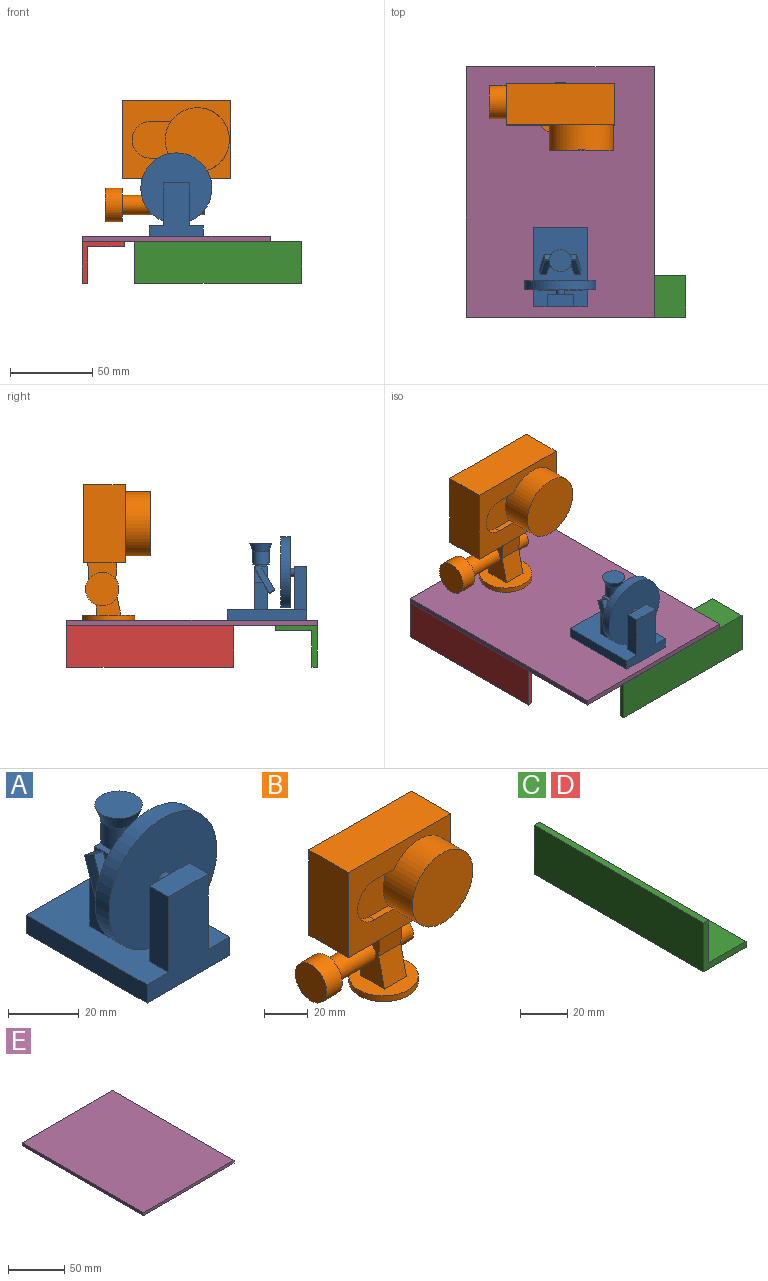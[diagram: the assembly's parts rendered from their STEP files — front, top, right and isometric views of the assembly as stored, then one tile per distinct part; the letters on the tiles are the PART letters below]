
ASSEMBLY  parts=5 mates=4
PART A: 46 faces, bbox 43.2x48.3x50.8 mm
  f0: plane 8.44x4.96mm, normal (-0.98,0,0.18), area 21.3mm2, adj f17,f20,f39
  f1: plane 3.03x1.72mm, normal (-0.98,0,0.18), area 2.6mm2, adj f20,f25,f43
  f2: plane 7.17x4.21mm, normal (0.98,0,0.18), area 15.4mm2, adj f18,f25,f33
  f3: plane 48.26x6.35mm, normal (-1,0,0), area 306.5mm2, adj f4,f6,f7,f8
  f4: plane 33.02x32.51mm, normal (0,-1,0), area 628.3mm2, adj f3,f5,f7,f8,f9,f10,f11
  f5: plane 48.26x6.35mm, normal (1,0,0), area 306.5mm2, adj f4,f6,f7,f8
  f6: plane 33.02x6.35mm, normal (0,1,0), area 209.7mm2, adj f3,f5,f7,f8
  f7: plane 48.26x33.02mm, normal (0,0,1), area 1374.8mm2, adj f3,f4,f5,f6,f9,f10,f12,f17
  f8: plane 48.26x33.02mm, normal (0,0,-1), area 1593.5mm2, adj f3,f4,f5,f6
  f9: plane 26.16x7.62mm, normal (-1,0,0), area 199.4mm2, adj f4,f7,f11,f12
  f10: plane 26.16x7.62mm, normal (1,0,0), area 199.4mm2, adj f4,f7,f11,f12
  f11: plane 16x7.62mm, normal (0,0,1), area 121.9mm2, adj f4,f9,f10,f12
  f12: plane 26.16x16mm, normal (0,1,0), area 398.4mm2, adj f7,f9,f10,f11,f13
  f13: cylinder r=2.54mm len=5.08mm, axis (0,-1,0), area 40.5mm2, adj f12,f16
  f14: cylinder r=21.59mm len=43.18mm, axis (0,-1,0), area 758mm2, adj f15,f16
  f15: plane 43.18x43.18mm, normal (0,1,0), area 1464.4mm2, adj f14
  f16: plane 43.18x43.18mm, normal (0,-1,0), area 1444.1mm2, adj f13,f14
  f17: plane 16.51x7.62mm, normal (-1,0,0), area 125.8mm2, adj f0,f7,f18,f20,f45
  f18: plane 26.67x15.24mm, normal (0,-1,0), area 361.3mm2, adj f2,f7,f17,f19,f21,f22,f23,f24
  f19: plane 10.16x7.62mm, normal (1,0,0), area 77.4mm2, adj f7,f18,f20,f23
  f20: plane 26.67x15.24mm, normal (0,1,0), area 361.3mm2, adj f0,f1,f7,f17,f19,f21,f22,f23
  f21: plane 10.16x7.62mm, normal (-1,0,0), area 77.4mm2, adj f7,f18,f20,f23
  f22: plane 16.51x7.62mm, normal (1,0,0), area 125.8mm2, adj f7,f18,f20,f26,f38
  f23: plane 7.62x2.54mm, normal (0,0,-1), area 19.4mm2, adj f18,f19,f20,f21
  f24: plane 7.2x4.23mm, normal (-0.98,0,0.18), area 15.5mm2, adj f18,f25,f41
  f25: plane 11.43x7.62mm, normal (0,0,1), area 47.4mm2, adj f1,f2,f18,f20,f24,f26,f27,f32
  f26: plane 10.16x4.98mm, normal (0.98,0,0.18), area 24.1mm2, adj f20,f22,f25,f35,f36
  f27: cylinder r=3.56mm len=7.11mm, axis (0,0,-1), area 28.4mm2, adj f25,f29
  f28: cylinder r=5.08mm len=10.16mm, axis (0,0,-1), area 243.2mm2, adj f29,f30
  f29: plane 10.16x10.16mm, normal (0,0,-1), area 41.3mm2, adj f27,f28
  f30: cone r=5.08mm half-angle=20deg, axis (0,0,1), area 180.7mm2, adj f28,f31
  f31: plane 13.49x13.49mm, normal (0,0,1), area 142.9mm2, adj f30
  f32: plane 3.74x0.7mm, normal (-0.18,0,0.98), area 1.4mm2, adj f25,f33,f36,f37
  f33: plane 15.65x8.78mm, normal (-0.09,-0.87,0.49), area 66.9mm2, adj f2,f32,f34,f37,f38
  f34: plane 4.1x3.3mm, normal (0.16,-0.5,-0.85), area 14.5mm2, adj f33,f35,f37,f38
  f35: plane 15.81x8.88mm, normal (0.09,0.87,-0.49), area 67.6mm2, adj f26,f34,f36,f37,f38
  f36: plane 4.07x3.02mm, normal (-0.16,0.5,0.85), area 13.3mm2, adj f26,f32,f35,f37
  f37: plane 16.82x12.18mm, normal (0.98,0,0.18), area 67.6mm2, adj f32,f33,f34,f35,f36
  f38: plane 9.66x7.21mm, normal (-0.98,0,-0.18), area 28.3mm2, adj f18,f22,f33,f34,f35
  f39: plane 15.84x8.89mm, normal (-0.09,0.87,-0.49), area 67.7mm2, adj f0,f40,f43,f44,f45
  f40: plane 4.1x3.3mm, normal (-0.16,-0.5,-0.85), area 14.5mm2, adj f39,f41,f44,f45
  f41: plane 15.68x8.8mm, normal (0.09,-0.87,0.49), area 67mm2, adj f24,f40,f42,f44,f45
  f42: plane 3.74x0.7mm, normal (0.18,0,0.98), area 1.4mm2, adj f25,f41,f43,f44
  f43: plane 4.07x3.03mm, normal (0.16,0.5,0.85), area 13.3mm2, adj f1,f39,f42,f44
  f44: plane 16.85x12.19mm, normal (-0.98,0,0.18), area 67.7mm2, adj f39,f40,f41,f42,f43
  f45: plane 9.65x7.23mm, normal (0.98,0,-0.18), area 28.4mm2, adj f17,f18,f39,f40,f41
PART B: 33 faces, bbox 76.2x41.3x82.6 mm
  f0: plane 66.04x47.63mm, normal (0,1,0), area 2919.3mm2, adj f1,f2,f3,f4,f12,f13,f14,f15
  f1: plane 47.63x25.4mm, normal (-1,0,0), area 1209.7mm2, adj f0,f2,f4,f5
  f2: plane 66.04x25.4mm, normal (0,0,-1), area 1424.5mm2, adj f0,f1,f3,f5,f17,f18,f22,f23
  f3: plane 47.63x25.4mm, normal (1,0,0), area 1209.7mm2, adj f0,f2,f4,f5
  f4: plane 66.04x25.4mm, normal (0,0,1), area 1677.4mm2, adj f0,f1,f3,f5
  f5: plane 66.04x47.63mm, normal (0,-1,0), area 1524.4mm2, adj f1,f2,f3,f4,f6,f8,f9,f10
  f6: cylinder r=19.56mm len=39.12mm, axis (0,1,0), area 1956.8mm2, adj f5,f7,f9,f10,f11
  f7: plane 39.12x39.12mm, normal (0,-1,0), area 1201.7mm2, adj f6
  f8: cylinder r=11.11mm len=22.23mm, axis (0,-1,0), area 124.1mm2, adj f5,f9,f10,f11
  f9: plane 12.48x3.56mm, normal (0,0,1), area 44.4mm2, adj f5,f6,f8,f11
  f10: plane 12.48x3.56mm, normal (0,0,-1), area 44.4mm2, adj f5,f6,f8,f11
  f11: plane 23.59x22.23mm, normal (0,-1,0), area 419.1mm2, adj f6,f8,f9,f10
  f12: plane 8.89x1.78mm, normal (0,0,-1), area 15.8mm2, adj f0,f13,f15,f16
  f13: plane 25.4x1.78mm, normal (-1,0,0), area 45.2mm2, adj f0,f12,f14,f16
  f14: plane 8.89x1.78mm, normal (0,0,1), area 15.8mm2, adj f0,f13,f15,f16
  f15: plane 25.4x1.78mm, normal (1,0,0), area 45.2mm2, adj f0,f12,f14,f16
  f16: plane 25.4x8.89mm, normal (0,1,0), area 225.8mm2, adj f12,f13,f14,f15
  f17: plane 16.46x14.22mm, normal (0,1,-0.08), area 234.8mm2, adj f2,f21,f22,f23
  f18: plane 15.33x14.22mm, normal (0,-1,-0.08), area 218.7mm2, adj f2,f19,f22,f23
  f19: plane 16.42x14.22mm, normal (0,-0.98,0.22), area 239.5mm2, adj f18,f22,f23,f30
  f20: plane 14.22x9.28mm, normal (0,1,0), area 132mm2, adj f21,f22,f23,f30
  f21: cylinder r=7.62mm len=14.22mm, axis (-1,0,0), area 105mm2, adj f17,f20,f22,f23
  f22: plane 31.75x20.27mm, normal (1,0,0), area 386.2mm2, adj f2,f17,f18,f19,f20,f21,f24,f30
  f23: plane 31.75x20.27mm, normal (-1,0,0), area 386.2mm2, adj f2,f17,f18,f19,f20,f21,f26,f30
  f24: cylinder r=5.84mm len=11.68mm, axis (-1,0,0), area 372.9mm2, adj f22,f25
  f25: plane 11.68x11.68mm, normal (1,0,0), area 107.2mm2, adj f24
  f26: cylinder r=5.84mm len=25.91mm, axis (1,0,0), area 951mm2, adj f23,f29
  f27: cylinder r=10.16mm len=20.32mm, axis (1,0,0), area 648.6mm2, adj f28,f29
  f28: plane 20.32x20.32mm, normal (-1,0,0), area 324.3mm2, adj f27
  f29: plane 20.32x20.32mm, normal (1,0,0), area 217.1mm2, adj f26,f27
  f30: plane 31.75x31.75mm, normal (0,0,1), area 575.2mm2, adj f19,f20,f22,f23,f31
  f31: cylinder r=15.88mm len=31.75mm, axis (0,0,-1), area 316.7mm2, adj f30,f32
  f32: plane 31.75x31.75mm, normal (0,0,-1), area 791.7mm2, adj f31
PART C: 8 faces, bbox 25.4x101.6x25.4 mm
  f0: plane 101.6x25.4mm, normal (-1,0,0), area 2580.6mm2, adj f1,f5,f6,f7
  f1: plane 101.6x25.4mm, normal (0,0,-1), area 2580.6mm2, adj f0,f2,f6,f7
  f2: plane 101.6x3.18mm, normal (1,0,0), area 322.6mm2, adj f1,f3,f6,f7
  f3: plane 101.6x22.23mm, normal (0,0,1), area 2258.1mm2, adj f2,f4,f6,f7
  f4: plane 101.6x22.23mm, normal (1,0,0), area 2258.1mm2, adj f3,f5,f6,f7
  f5: plane 101.6x3.18mm, normal (0,0,1), area 322.6mm2, adj f0,f4,f6,f7
  f6: plane 25.4x25.4mm, normal (0,-1,0), area 151.2mm2, adj f0,f1,f2,f3,f4,f5
  f7: plane 25.4x25.4mm, normal (0,1,0), area 151.2mm2, adj f0,f1,f2,f3,f4,f5
PART D: same geometry as C
PART E: 6 faces, bbox 114.3x152.4x3.2 mm
  f0: plane 152.4x3.18mm, normal (-1,0,0), area 483.9mm2, adj f1,f3,f4,f5
  f1: plane 114.3x3.18mm, normal (0,-1,0), area 362.9mm2, adj f0,f2,f4,f5
  f2: plane 152.4x3.18mm, normal (1,0,0), area 483.9mm2, adj f1,f3,f4,f5
  f3: plane 114.3x3.18mm, normal (0,1,0), area 362.9mm2, adj f0,f2,f4,f5
  f4: plane 152.4x114.3mm, normal (0,0,1), area 17419.3mm2, adj f0,f1,f2,f3
  f5: plane 152.4x114.3mm, normal (0,0,-1), area 17419.3mm2, adj f0,f1,f2,f3
PLACE A t=(57.15,6.35,3.18)mm
PLACE B t=(57.15,116.84,3.18)mm
PLACE C rot(axis=(-0.58,0.58,0.58),120deg) t=(31.75,0,0)mm
PLACE D rot(axis=(0,1,0),90deg) t=(0,152.4,0)mm
PLACE E at identity
MATE fastened C.f0 <-> E.f5  axis (0,0,1) through (82.55,0,0)mm
MATE fastened A.f8 <-> E.f4  axis (0,0,-1) through (57.15,6.35,3.18)mm
MATE fastened B.f31 <-> E.f4  axis (0,0,-1) through (57.15,127,3.18)mm
MATE fastened D.f0 <-> E.f5  axis (0,0,1) through (0,101.6,0)mm
